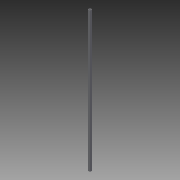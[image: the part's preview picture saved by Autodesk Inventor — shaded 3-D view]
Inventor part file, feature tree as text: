
AUTODESK INVENTOR PART (.ipt)
format: ipt  version: 2013 (Build 170138000, 138)  size: 77,312 bytes
history: native  units: in
note: dims shown in document units (in); Inventor stores cm internally (conversion verified against a paired STEP export)
features: other x2, extrude x1, sketch x1
ambient origin geometry x8: Origin, YZ Plane, XZ Plane, XY Plane, X Axis, Y Axis, Z Axis, Center Point
bodies: Solid1 (feature_tree)
feature tree (4):
  other  "Table"
  other  "Part15-01"
  extrude  "Extrusion1"  Depth=1.0in
  sketch  "Sketch1"  dims[d0=1.0in d1=1.0in d2=0.125in d4=0.0in]
